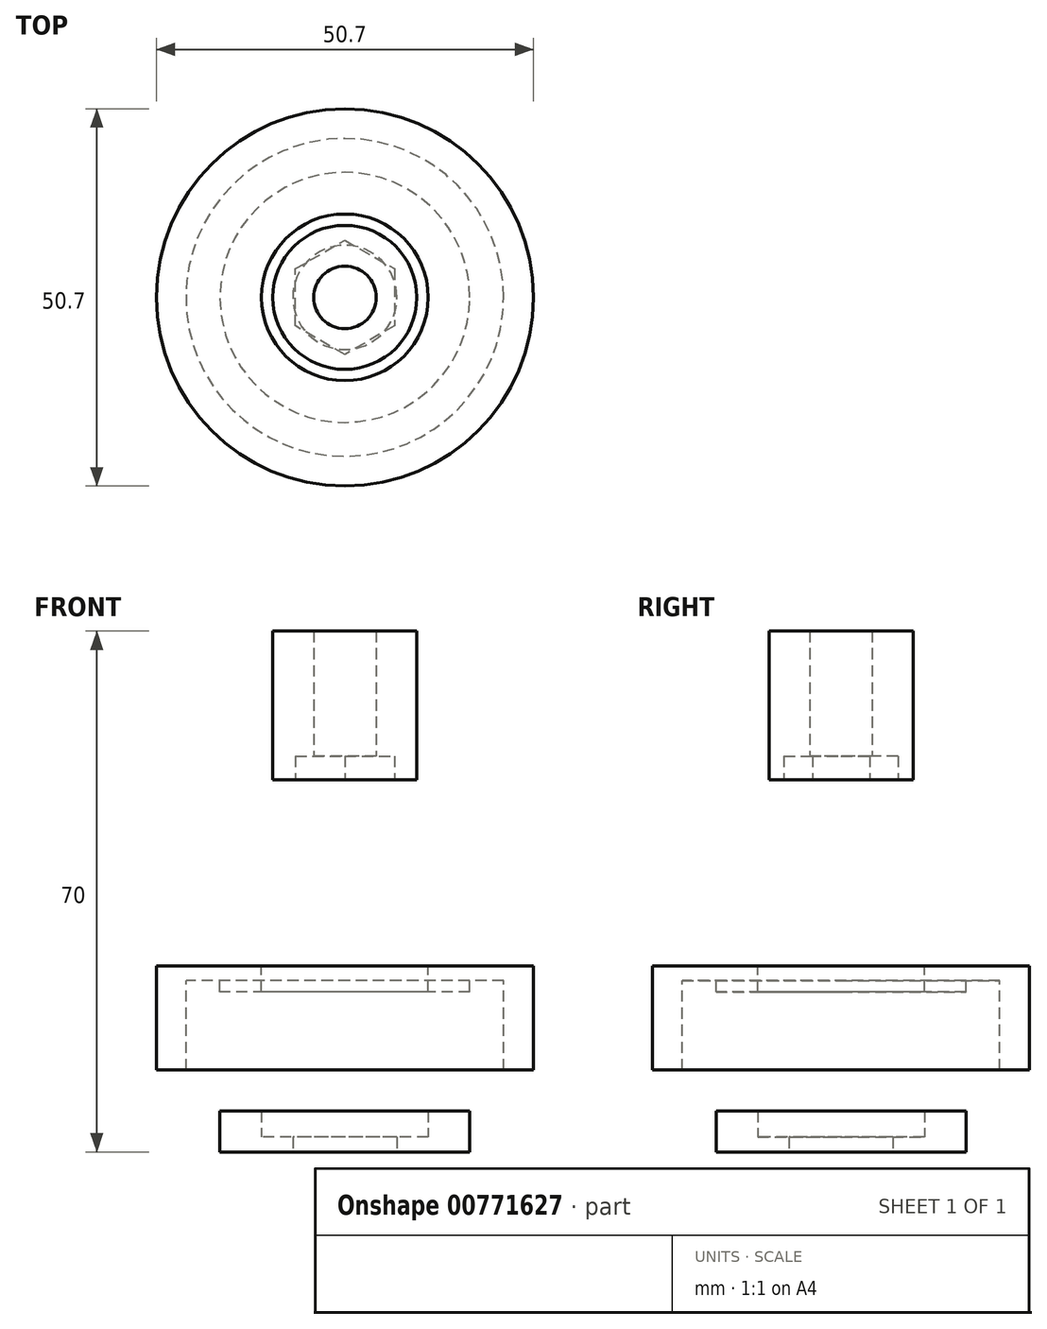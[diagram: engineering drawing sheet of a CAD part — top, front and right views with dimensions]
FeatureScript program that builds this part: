
annotation { "Feature Type Name" : "Feature", "Feature Type Description" : "" }
export const myFeature = defineFeature(function(context is Context, id is Id, definition is map)
    precondition{}
    {
        {
            assignVariable(context, id + "F0", {"variableType" : VariableType.LENGTH, "name" : "Bearing_T", "lengthValue" : 7 * mm});
        }
        {
            assignVariable(context, id + "F1", {"variableType" : VariableType.LENGTH, "name" : "Min_Wall_T", "lengthValue" : 2 * mm});
        }
        {
            assignVariable(context, id + "F2", {"variableType" : VariableType.LENGTH, "name" : "M8_Nut_T", "lengthValue" : (0.8 * 8) * mm});
        }
        {
            assignVariable(context, id + "F3", {"variableType" : VariableType.LENGTH, "name" : "Spacer_L", "lengthValue" : 20 * mm});
        }
        {
            var Q0;
            Q0=qCreatedBy(makeId("Top.planeOp"),FACE);
            var sketch = newSketch(context, id + "F4", { "sketchPlane" : qUnion([Q0])});
            skCircle(sketch, "E0", {"center": v(0, 0) * mm, "radius": 7 * mm});
            skCircle(sketch, "E1", {"center": v(0, 0) * mm, "radius": 16.8 * mm});
            skCircle(sketch, "E2", {"center": v(0, 0) * mm, "radius": 11.2 * mm});
            skSolve(sketch);
        }
        {
            var Q0;
            Q0=makeQuery(id+"F4.imprint","IMPRINT",FACE,{"disambiguationData":[TD([[makeQuery(id+"F4.imprint","IMPRINT",EDGE,{"derivedFrom":sQuery(id+"F4.wireOp",EDGE,"E0")}),-1.0]])]});
            var Q1;
            Q1=makeQuery(id+"F4.imprint","IMPRINT",FACE,{"disambiguationData":[TD([[makeQuery(id+"F4.imprint","IMPRINT",EDGE,{"derivedFrom":sQuery(id+"F4.wireOp",EDGE,"E1")}),1.0]])]});
            extrude(context, id + "F5", {"entities" : qUnion([Q0, Q1]), "depth" : getVariable(context, 'Min_Wall_T'), "offsetDistance" : 25 * mm});
        }
        {
            var Q0;
            Q0=makeQuery(id+"F4.imprint","IMPRINT",FACE,{"disambiguationData":[TD([[makeQuery(id+"F4.imprint","IMPRINT",EDGE,{"derivedFrom":sQuery(id+"F4.wireOp",EDGE,"E1")}),1.0]])]});
            extrude(context, id + "F6", {"entities" : qUnion([Q0]), "operationType" : NewBodyOperationType.ADD, "depth" : (getVariable(context, 'Bearing_T') / 2) + getVariable(context, 'Min_Wall_T'), "offsetDistance" : 25 * mm});
        }
        {
            var Q0;
            Q0=qCreatedBy(makeId("Top.planeOp"),FACE);
            cPlane(context, id + "F7", {"entities" : qUnion([Q0]), "cplaneType" : CPlaneType.OFFSET, "offset" : 25 * mm, "width" : 150 * mm, "height" : 150 * mm});
        }
        {
            var Q0;
            Q0=qCreatedBy(id+"F7.planeOp",FACE);
            var sketch = newSketch(context, id + "F8", { "sketchPlane" : qUnion([Q0])});
            skCircle(sketch, "E3", {"center": v(0, 0) * mm, "radius": 21.35 * mm});
            skCircle(sketch, "E4.0", {"center": v(0, 0) * mm, "radius": 25.35 * mm});
            skCircle(sketch, "E5.0", {"center": v(0, 0) * mm, "radius": 16.8 * mm});
            skCircle(sketch, "E6.0", {"center": v(0, 0) * mm, "radius": 11.2 * mm});
            skSolve(sketch);
        }
        {
            var Q0;
            Q0=makeQuery(id+"F8.imprint","IMPRINT",FACE,{"disambiguationData":[TD([[makeQuery(id+"F8.imprint","IMPRINT",EDGE,{"derivedFrom":sQuery(id+"F8.wireOp",EDGE,"E5.0")}),1.0]])]});
            extrude(context, id + "F9", {"entities" : qUnion([Q0]), "oppositeDirection" : true, "depth" : (getVariable(context, 'Bearing_T') / 2), "offsetDistance" : 25 * mm});
        }
        {
            var Q0;
            Q0=makeQuery(id+"F8.imprint","IMPRINT",FACE,{"disambiguationData":[TD([[makeQuery(id+"F8.imprint","IMPRINT",EDGE,{"derivedFrom":sQuery(id+"F8.wireOp",EDGE,"E3")}),1.0]])]});
            extrude(context, id + "F10", {"entities" : qUnion([Q0]), "operationType" : NewBodyOperationType.ADD, "oppositeDirection" : true, "depth" : getVariable(context, 'Min_Wall_T'), "offsetDistance" : 25 * mm});
        }
        {
            var Q0;
            Q0 = qSketchRegion(id + "F8", true);
            extrude(context, id + "F11", {"entities" : qUnion([Q0]), "operationType" : NewBodyOperationType.ADD, "oppositeDirection" : true, "depth" : getVariable(context, 'Min_Wall_T') + getVariable(context, 'Bearing_T') + 5 * mm, "offsetDistance" : 25 * mm});
        }
        {
            var Q0;
            Q0=qCreatedBy(id+"F7.planeOp",FACE);
            cPlane(context, id + "F12", {"entities" : qUnion([Q0]), "cplaneType" : CPlaneType.OFFSET, "offset" : 25 * mm, "width" : 150 * mm, "height" : 150 * mm});
        }
        {
            var Q0;
            Q0=qCreatedBy(id+"F12.planeOp",FACE);
            var sketch = newSketch(context, id + "F13", { "sketchPlane" : qUnion([Q0])});
            skCircle(sketch, "E7.cCircle", {"center": v(0, 0) * mm, "radius": 6.65 * mm, "construction": true});
            skLineSegment(sketch, "E7.0", {"start": v(6.65, 3.84) * mm, "end": v(6.65, -3.84) * mm});
            skLineSegment(sketch, "E7.1", {"start": v(6.65, -3.84) * mm, "end": v(0, -7.68) * mm});
            skLineSegment(sketch, "E7.2", {"start": v(0, -7.68) * mm, "end": v(-6.65, -3.84) * mm});
            skLineSegment(sketch, "E7.3", {"start": v(-6.65, -3.84) * mm, "end": v(-6.65, 3.84) * mm});
            skLineSegment(sketch, "E7.4", {"start": v(-6.65, 3.84) * mm, "end": v(0, 7.68) * mm});
            skLineSegment(sketch, "E7.5", {"start": v(0, 7.68) * mm, "end": v(6.65, 3.84) * mm});
            skPoint(sketch, "E7.0.midPoint", {"position": v(6.65, 0) * mm});
            skCircle(sketch, "E8", {"center": v(0, 0) * mm, "radius": 9.68 * mm});
            skCircle(sketch, "E9.0", {"center": v(0, 0) * mm, "radius": 4.2 * mm});
            skSolve(sketch);
        }
        {
            var Q0;
            Q0=makeQuery(id+"F13.imprint","IMPRINT",FACE,{"disambiguationData":[TD([[makeQuery(id+"F13.imprint","IMPRINT",EDGE,{"derivedFrom":sQuery(id+"F13.wireOp",EDGE,"E7.0")}),1.0]])]});
            var Q1;
            Q1=makeQuery(id+"F13.imprint","IMPRINT",FACE,{"disambiguationData":[TD([[makeQuery(id+"F13.imprint","IMPRINT",EDGE,{"derivedFrom":sQuery(id+"F13.wireOp",EDGE,"E7.0")}),-1.0]])]});
            extrude(context, id + "F14", {"entities" : qUnion([Q0, Q1]), "depth" : getVariable(context, 'Spacer_L'), "offsetDistance" : 25 * mm});
        }
        {
            var Q0;
            Q0=makeQuery(id+"F13.imprint","IMPRINT",FACE,{"disambiguationData":[TD([[makeQuery(id+"F13.imprint","IMPRINT",EDGE,{"derivedFrom":sQuery(id+"F13.wireOp",EDGE,"E7.0")}),-1.0]])]});
            extrude(context, id + "F15", {"entities" : qUnion([Q0]), "operationType" : NewBodyOperationType.REMOVE, "depth" : getVariable(context, 'M8_Nut_T') / 2, "offsetDistance" : 25 * mm});
        }
    });
